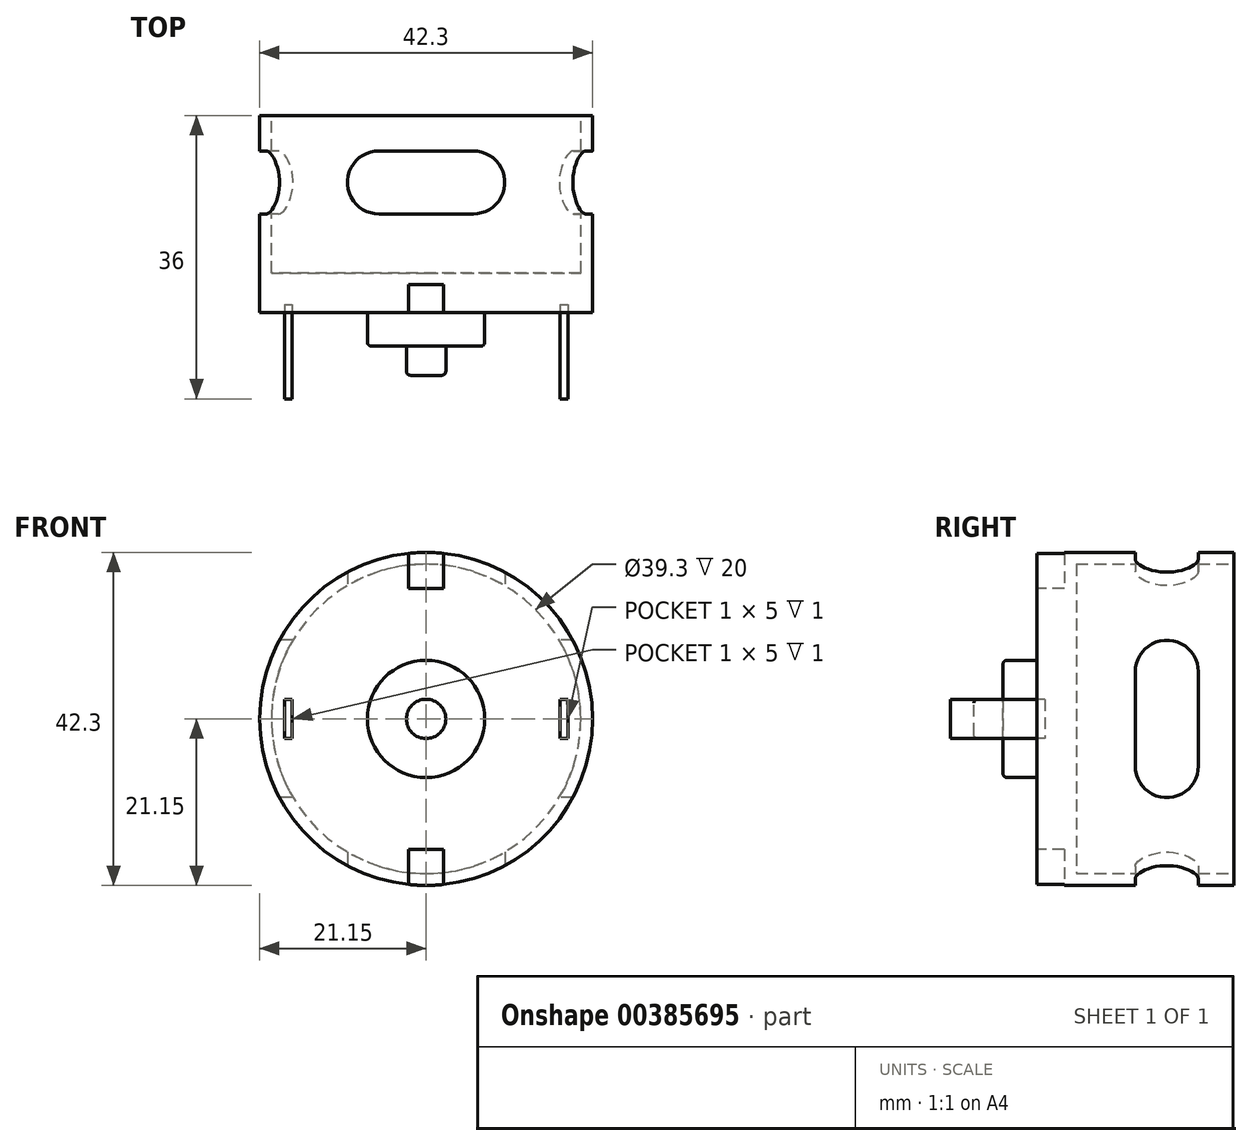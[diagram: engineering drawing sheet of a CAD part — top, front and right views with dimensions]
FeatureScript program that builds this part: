
annotation { "Feature Type Name" : "Feature", "Feature Type Description" : "" }
export const myFeature = defineFeature(function(context is Context, id is Id, definition is map)
    precondition{}
    {
        {
            var Q0;
            Q0=qCreatedBy(makeId("Front.planeOp"),FACE);
            var sketch = newSketch(context, id + "F0", { "sketchPlane" : qUnion([Q0])});
            skCircle(sketch, "E0", {"center": v(0, 0) * mm, "radius": 21.15 * mm});
            skPoint(sketch, "E1", {"position": v(21.15, 0) * mm});
            skPoint(sketch, "E2", {"position": v(-21.15, 0) * mm});
            skLineSegment(sketch, "E3", {"start": v(-21.15, 0) * mm, "end": v(21.15, 0) * mm, "construction": true});
            skPoint(sketch, "E4", {"position": v(-17.5, 0) * mm});
            skPoint(sketch, "E5", {"position": v(17.5, 0) * mm});
            skLineSegment(sketch, "E6.bottom", {"start": v(17, 2.5) * mm, "end": v(18, 2.5) * mm});
            skLineSegment(sketch, "E6.top", {"start": v(17, -2.5) * mm, "end": v(18, -2.5) * mm});
            skLineSegment(sketch, "E6.left", {"start": v(17, 2.5) * mm, "end": v(17, -2.5) * mm});
            skLineSegment(sketch, "E6.right", {"start": v(18, 2.5) * mm, "end": v(18, -2.5) * mm});
            skLineSegment(sketch, "E7.bottom", {"start": v(-18, 2.5) * mm, "end": v(-17, 2.5) * mm});
            skLineSegment(sketch, "E7.top", {"start": v(-18, -2.5) * mm, "end": v(-17, -2.5) * mm});
            skLineSegment(sketch, "E7.left", {"start": v(-18, 2.5) * mm, "end": v(-18, -2.5) * mm});
            skLineSegment(sketch, "E7.right", {"start": v(-17, 2.5) * mm, "end": v(-17, -2.5) * mm});
            skSolve(sketch);
        }
        {
            var Q0;
            Q0=makeQuery(id+"F0.imprint","IMPRINT",FACE,{"disambiguationData":[TD([[makeQuery(id+"F0.imprint","IMPRINT",EDGE,{"derivedFrom":sQuery(id+"F0.wireOp",EDGE,"E7.bottom")}),-1.0]])]});
            var Q1;
            Q1=makeQuery(id+"F0.imprint","IMPRINT",FACE,{"disambiguationData":[TD([[makeQuery(id+"F0.imprint","IMPRINT",EDGE,{"derivedFrom":sQuery(id+"F0.wireOp",EDGE,"E6.bottom")}),-1.0]])]});
            extrude(context, id + "F1", {"entities" : qUnion([Q0, Q1]), "depth" : 11 * mm});
        }
        {
            var Q0;
            Q0=makeQuery(id+"F0.imprint","IMPRINT",FACE,{"disambiguationData":[TD([[makeQuery(id+"F0.imprint","IMPRINT",EDGE,{"derivedFrom":sQuery(id+"F0.wireOp",EDGE,"E0")}),1.0]])]});
            var Q1;
            Q1=makeQuery(id+"F0.imprint","IMPRINT",FACE,{"disambiguationData":[TD([[makeQuery(id+"F0.imprint","IMPRINT",EDGE,{"derivedFrom":sQuery(id+"F0.wireOp",EDGE,"E7.bottom")}),-1.0]])]});
            var Q2;
            Q2=makeQuery(id+"F0.imprint","IMPRINT",FACE,{"disambiguationData":[TD([[makeQuery(id+"F0.imprint","IMPRINT",EDGE,{"derivedFrom":sQuery(id+"F0.wireOp",EDGE,"E6.bottom")}),-1.0]])]});
            extrude(context, id + "F2", {"entities" : qUnion([Q0, Q1, Q2]), "oppositeDirection" : true, "depth" : 25 * mm});
        }
        {
            var Q0;
            Q0=makeQuery(id+"F2.opExtrude","CAP_FACE",FACE,{"disambiguationData":[OSD([sQuery(id+"F0.wireOp",EDGE,"E0"),sQuery(id+"F0.wireOp",EDGE,"E6.bottom"),sQuery(id+"F0.wireOp",EDGE,"E6.top"),sQuery(id+"F0.wireOp",EDGE,"E6.left"),sQuery(id+"F0.wireOp",EDGE,"E6.right"),sQuery(id+"F0.wireOp",EDGE,"E7.bottom"),sQuery(id+"F0.wireOp",EDGE,"E7.top"),sQuery(id+"F0.wireOp",EDGE,"E7.left"),sQuery(id+"F0.wireOp",EDGE,"E7.right")])],"isStart":false});
            var sketch = newSketch(context, id + "F3", { "sketchPlane" : qUnion([Q0])});
            skCircle(sketch, "E8", {"center": v(0, 0) * mm, "radius": 19.65 * mm});
            skSolve(sketch);
        }
        {
            var Q0;
            Q0=qSketchRegion(id+"F3",true);
            extrude(context, id + "F4", {"entities" : qUnion([Q0]), "operationType" : NewBodyOperationType.REMOVE, "oppositeDirection" : true, "depth" : 20 * mm});
        }
        {
            var Q0;
            Q0=qCreatedBy(makeId("Right.planeOp"),FACE);
            var sketch = newSketch(context, id + "F5", { "sketchPlane" : qUnion([Q0])});
            skPoint(sketch, "E9", {"position": v(16.5, 0) * mm});
            skLineSegment(sketch, "E10.bottom", {"start": v(20.5, 10) * mm, "end": v(12.5, 10) * mm});
            skLineSegment(sketch, "E10.top", {"start": v(20.5, -10) * mm, "end": v(12.5, -10) * mm});
            skLineSegment(sketch, "E10.left", {"start": v(20.5, 10) * mm, "end": v(20.5, -10) * mm});
            skLineSegment(sketch, "E10.right", {"start": v(12.5, 10) * mm, "end": v(12.5, -10) * mm});
            skPoint(sketch, "E11", {"position": v(16.5, 6) * mm});
            skPoint(sketch, "E12", {"position": v(16.5, -6) * mm});
            skArc(sketch, "E13", {"start": v(12.5, 6) * mm, "mid": v(16.5, 10) * mm, "end": v(20.5, 6) * mm});
            skArc(sketch, "E14", {"start": v(20.5, -6) * mm, "mid": v(16.5, -10) * mm, "end": v(12.5, -6) * mm});
            skSolve(sketch);
        }
        {
            var Q0;
            {var subQ0=sQuery(id+"F5.wireOp",EDGE,"E13");var subQ1=sQuery(id+"F5.wireOp",EDGE,"E10.left");var subQ2=makeQuery(id+"F5.imprint","INTERSECT",VERTEX,{"derivedFrom":[subQ1,subQ0]});Q0=makeQuery(id+"F5.imprint","IMPRINT",FACE,{"disambiguationData":[TD([[makeQuery(id+"F5.imprint","IMPRINT",EDGE,{"disambiguationData":[TD([[subQ2,-1.0]])],"derivedFrom":subQ1}),-1.0]])]});}
            extrude(context, id + "F6", {"entities" : qUnion([Q0]), "operationType" : NewBodyOperationType.REMOVE, "endBound" : BoundingType.SYMMETRIC, "depth" : 45 * mm});
        }
        {
            var Q0;
            Q0=qCreatedBy(makeId("Top.planeOp"),FACE);
            var sketch = newSketch(context, id + "F7", { "sketchPlane" : qUnion([Q0])});
            skPoint(sketch, "E15", {"position": v(0, 16.5) * mm});
            skLineSegment(sketch, "E16.bottom", {"start": v(-10, 20.5) * mm, "end": v(10, 20.5) * mm});
            skLineSegment(sketch, "E16.top", {"start": v(-10, 12.5) * mm, "end": v(10, 12.5) * mm});
            skLineSegment(sketch, "E16.left", {"start": v(-10, 20.5) * mm, "end": v(-10, 12.5) * mm});
            skLineSegment(sketch, "E16.right", {"start": v(10, 20.5) * mm, "end": v(10, 12.5) * mm});
            skPoint(sketch, "E17", {"position": v(6, 16.5) * mm});
            skPoint(sketch, "E18", {"position": v(-6, 16.5) * mm});
            skArc(sketch, "E19", {"start": v(-6, 12.5) * mm, "mid": v(-10, 16.5) * mm, "end": v(-6, 20.5) * mm});
            skArc(sketch, "E20", {"start": v(6, 20.5) * mm, "mid": v(10, 16.5) * mm, "end": v(6, 12.5) * mm});
            skSolve(sketch);
        }
        {
            var Q0;
            {var subQ0=sQuery(id+"F7.wireOp",EDGE,"E19");var subQ6=sQuery(id+"F7.wireOp",EDGE,"E16.bottom");var subQ7=makeQuery(id+"F7.imprint","INTERSECT",VERTEX,{"derivedFrom":[subQ6,subQ0]});Q0=makeQuery(id+"F7.imprint","IMPRINT",FACE,{"disambiguationData":[TD([[makeQuery(id+"F7.imprint","IMPRINT",EDGE,{"disambiguationData":[TD([[subQ7,-1.0]])],"derivedFrom":subQ6}),-1.0]])]});}
            extrude(context, id + "F8", {"entities" : qUnion([Q0]), "operationType" : NewBodyOperationType.REMOVE, "endBound" : BoundingType.SYMMETRIC, "depth" : 45 * mm});
        }
        {
            var Q0;
            Q0=makeQuery(id+"F2.opExtrude","CAP_FACE",FACE,{"disambiguationData":[OSD([sQuery(id+"F0.wireOp",EDGE,"E0"),sQuery(id+"F0.wireOp",EDGE,"E6.bottom"),sQuery(id+"F0.wireOp",EDGE,"E6.top"),sQuery(id+"F0.wireOp",EDGE,"E6.left"),sQuery(id+"F0.wireOp",EDGE,"E6.right"),sQuery(id+"F0.wireOp",EDGE,"E7.bottom"),sQuery(id+"F0.wireOp",EDGE,"E7.top"),sQuery(id+"F0.wireOp",EDGE,"E7.left"),sQuery(id+"F0.wireOp",EDGE,"E7.right")])],"isStart":true});
            var sketch = newSketch(context, id + "F9", { "sketchPlane" : qUnion([Q0])});
            skPoint(sketch, "E21", {"position": v(0, 21.15) * mm});
            skPoint(sketch, "E22", {"position": v(0, -21.15) * mm});
            skLineSegment(sketch, "E23.bottom", {"start": v(-2.2, -16.55) * mm, "end": v(2.2, -16.55) * mm});
            skLineSegment(sketch, "E23.top", {"start": v(-2.2, -25.75) * mm, "end": v(2.2, -25.75) * mm});
            skLineSegment(sketch, "E23.left", {"start": v(-2.2, -16.55) * mm, "end": v(-2.2, -25.75) * mm});
            skLineSegment(sketch, "E23.right", {"start": v(2.2, -16.55) * mm, "end": v(2.2, -25.75) * mm});
            skLineSegment(sketch, "E24.bottom", {"start": v(-2.2, 25.75) * mm, "end": v(2.2, 25.75) * mm});
            skLineSegment(sketch, "E24.top", {"start": v(-2.2, 16.55) * mm, "end": v(2.2, 16.55) * mm});
            skLineSegment(sketch, "E24.left", {"start": v(-2.2, 25.75) * mm, "end": v(-2.2, 16.55) * mm});
            skLineSegment(sketch, "E24.right", {"start": v(2.2, 25.75) * mm, "end": v(2.2, 16.55) * mm});
            skCircle(sketch, "E25", {"center": v(0, 0) * mm, "radius": 21.15 * mm});
            skSolve(sketch);
        }
        {
            var Q0;
            {var subQ0=sQuery(id+"F9.wireOp",EDGE,"E24.top");Q0=makeQuery(id+"F9.imprint","IMPRINT",FACE,{"disambiguationData":[TD([[makeQuery(id+"F9.imprint","IMPRINT",EDGE,{"derivedFrom":subQ0}),1.0]])]});}
            var Q1;
            {var subQ0=sQuery(id+"F9.wireOp",EDGE,"E23.bottom");Q1=makeQuery(id+"F9.imprint","IMPRINT",FACE,{"disambiguationData":[TD([[makeQuery(id+"F9.imprint","IMPRINT",EDGE,{"derivedFrom":subQ0}),-1.0]])]});}
            extrude(context, id + "F10", {"entities" : qUnion([Q0, Q1]), "operationType" : NewBodyOperationType.REMOVE, "oppositeDirection" : true, "depth" : 3.5 * mm});
        }
        {
            var Q0;
            Q0=makeQuery(id+"F2.opExtrude","CAP_FACE",FACE,{"disambiguationData":[OSD([sQuery(id+"F0.wireOp",EDGE,"E0"),sQuery(id+"F0.wireOp",EDGE,"E6.bottom"),sQuery(id+"F0.wireOp",EDGE,"E6.top"),sQuery(id+"F0.wireOp",EDGE,"E6.left"),sQuery(id+"F0.wireOp",EDGE,"E6.right"),sQuery(id+"F0.wireOp",EDGE,"E7.bottom"),sQuery(id+"F0.wireOp",EDGE,"E7.top"),sQuery(id+"F0.wireOp",EDGE,"E7.left"),sQuery(id+"F0.wireOp",EDGE,"E7.right")])],"isStart":true});
            var sketch = newSketch(context, id + "F11", { "sketchPlane" : qUnion([Q0])});
            skCircle(sketch, "E26", {"center": v(0, 0) * mm, "radius": 7.45 * mm});
            skCircle(sketch, "E27", {"center": v(0, 0) * mm, "radius": 2.5 * mm});
            skSolve(sketch);
        }
        {
            var Q0;
            Q0=qSketchRegion(id+"F11",true);
            extrude(context, id + "F12", {"entities" : qUnion([Q0]), "operationType" : NewBodyOperationType.ADD, "depth" : 4.3 * mm});
        }
        {
            var Q0;
            Q0=makeQuery(id+"F12.boolean.opBoolean","SPLIT",FACE,{"disambiguationData":[TD([makeQuery(id+"F12.opExtrude","SWEPT_FACE",FACE,{"disambiguationData":[OSD([sQuery(id+"F11.wireOp",EDGE,"E27")])]})])],"derivedFrom":makeQuery(id+"F2.opExtrude","CAP_FACE",FACE,{"disambiguationData":[OSD([sQuery(id+"F0.wireOp",EDGE,"E0"),sQuery(id+"F0.wireOp",EDGE,"E6.bottom"),sQuery(id+"F0.wireOp",EDGE,"E6.top"),sQuery(id+"F0.wireOp",EDGE,"E6.left"),sQuery(id+"F0.wireOp",EDGE,"E6.right"),sQuery(id+"F0.wireOp",EDGE,"E7.bottom"),sQuery(id+"F0.wireOp",EDGE,"E7.top"),sQuery(id+"F0.wireOp",EDGE,"E7.left"),sQuery(id+"F0.wireOp",EDGE,"E7.right")])],"isStart":true})});
            extrude(context, id + "F13", {"entities" : qUnion([Q0]), "operationType" : NewBodyOperationType.ADD, "depth" : 8 * mm});
        }
        {
            var Q0;
            Q0=makeQuery(id+"F12.opExtrude","CAP_EDGE",EDGE,{"disambiguationData":[OSD([sQuery(id+"F11.wireOp",EDGE,"E26")])],"isStart":false});
            var Q1;
            Q1=makeQuery(id+"F13.opExtrude","CAP_EDGE",EDGE,{"disambiguationData":[OSD([sQuery(id+"F11.wireOp",EDGE,"E27")])],"isStart":false});
            fillet(context, id + "F14", {"entities" : qUnion([Q0, Q1]), "radius" : 0.5 * mm, "tangentPropagation" : true, "allowEdgeOverflow" : false});
        }
        {
            var Q0;
            Q0=makeQuery(id+"F0.imprint","IMPRINT",FACE,{"disambiguationData":[TD([[makeQuery(id+"F0.imprint","IMPRINT",EDGE,{"derivedFrom":sQuery(id+"F0.wireOp",EDGE,"E7.bottom")}),-1.0]])]});
            var Q1;
            Q1=makeQuery(id+"F0.imprint","IMPRINT",FACE,{"disambiguationData":[TD([[makeQuery(id+"F0.imprint","IMPRINT",EDGE,{"derivedFrom":sQuery(id+"F0.wireOp",EDGE,"E6.bottom")}),-1.0]])]});
            extrude(context, id + "F15", {"entities" : qUnion([Q0, Q1]), "operationType" : NewBodyOperationType.REMOVE, "oppositeDirection" : true, "depth" : 1 * mm});
        }
    });
